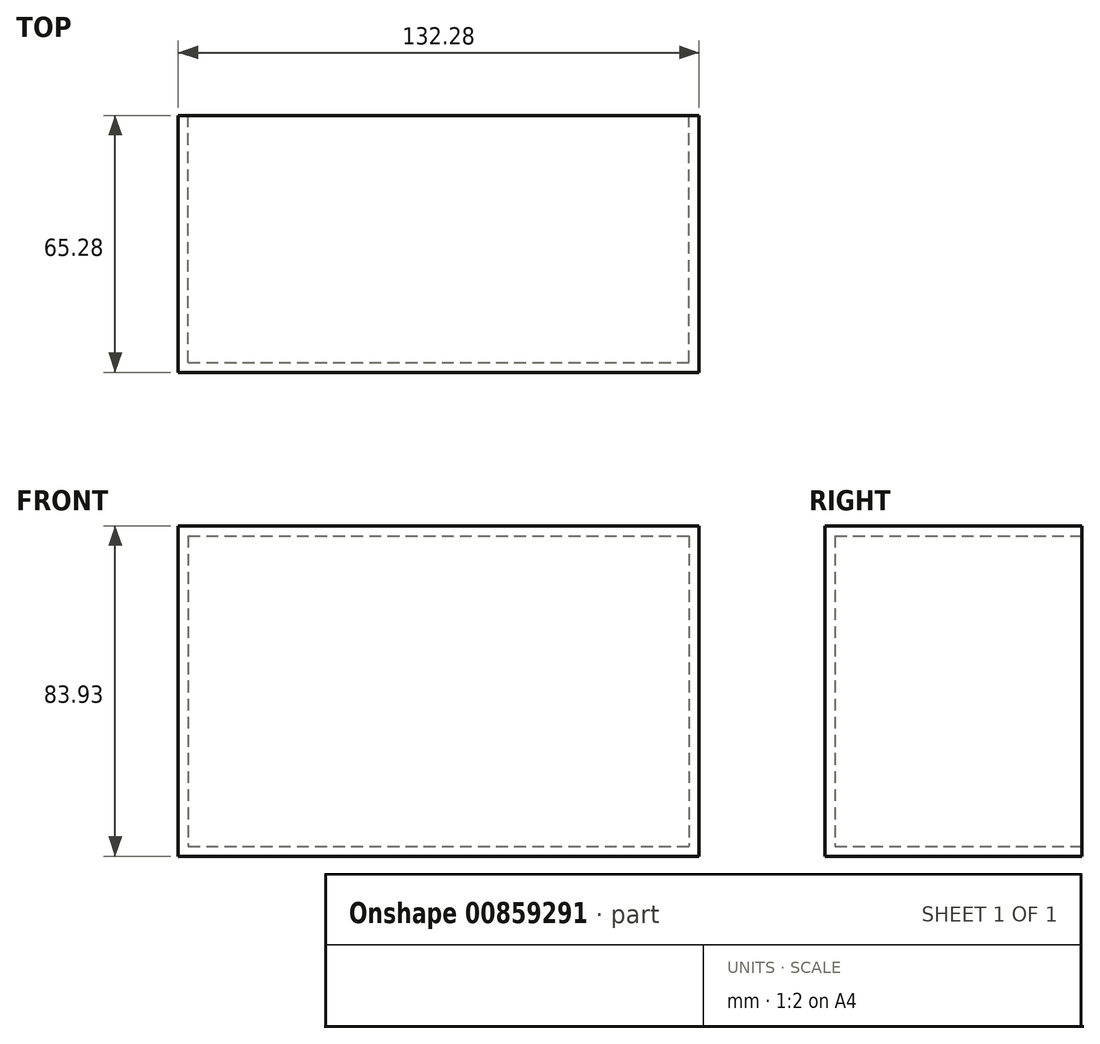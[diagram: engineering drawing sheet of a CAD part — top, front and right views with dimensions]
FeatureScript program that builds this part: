
annotation { "Feature Type Name" : "Feature", "Feature Type Description" : "" }
export const myFeature = defineFeature(function(context is Context, id is Id, definition is map)
    precondition{}
    {
        {
            var Q0;
            Q0=qCreatedBy(makeId("Front.planeOp"),FACE);
            var sketch = newSketch(context, id + "F0", { "sketchPlane" : qUnion([Q0])});
            skLineSegment(sketch, "E0.bottom", {"start": v(-60.6, 11.01) * mm, "end": v(71.68, 11.01) * mm});
            skLineSegment(sketch, "E0.top", {"start": v(-60.6, -72.92) * mm, "end": v(71.68, -72.92) * mm});
            skLineSegment(sketch, "E0.left", {"start": v(-60.6, 11.01) * mm, "end": v(-60.6, -72.92) * mm});
            skLineSegment(sketch, "E0.right", {"start": v(71.68, 11.01) * mm, "end": v(71.68, -72.92) * mm});
            skSolve(sketch);
        }
        {
            var Q0;
            Q0=makeQuery(id+"F0.imprint","IMPRINT",FACE,{"disambiguationData":[TD([[makeQuery(id+"F0.imprint","IMPRINT",EDGE,{"derivedFrom":sQuery(id+"F0.wireOp",EDGE,"E0.bottom")}),-1.0]])]});
            extrude(context, id + "F1", {"entities" : qUnion([Q0]), "depth" : 25.4 * mm, "offsetDistance" : 25.4 * mm});
        }
        {
            var Q0;
            Q0=makeQuery(id+"F1.opExtrude","CAP_FACE",FACE,{"disambiguationData":[OSD([sQuery(id+"F0.wireOp",EDGE,"E0.bottom"),sQuery(id+"F0.wireOp",EDGE,"E0.top"),sQuery(id+"F0.wireOp",EDGE,"E0.left"),sQuery(id+"F0.wireOp",EDGE,"E0.right")])],"isStart":true});
            extrude(context, id + "F2", {"entities" : qUnion([Q0]), "operationType" : NewBodyOperationType.ADD, "depth" : 39.88 * mm, "offsetDistance" : 25.4 * mm});
        }
        {
            var Q0;
            Q0=makeQuery(id+"F2.opExtrude","CAP_FACE",FACE,{"disambiguationData":[OSD([sQuery(id+"F0.wireOp",EDGE,"E0.bottom"),sQuery(id+"F0.wireOp",EDGE,"E0.top"),sQuery(id+"F0.wireOp",EDGE,"E0.left"),sQuery(id+"F0.wireOp",EDGE,"E0.right")])],"isStart":false});
            shell(context, id + "F3", {"entities" : qUnion([Q0]), "thickness" : 2.54 * mm});
        }
    });
